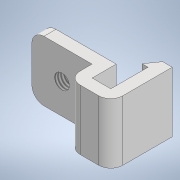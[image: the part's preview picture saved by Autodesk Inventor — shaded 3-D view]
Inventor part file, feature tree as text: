
AUTODESK INVENTOR PART (.ipt)
format: ipt  version: 2021 (Build 250183000, 183)  size: 137,216 bytes
history: native  units: mm
features: sketch x2, other x1, extrude x1, hole x1, fillet x1
ambient origin geometry x8: Origin, YZ Plane, XZ Plane, XY Plane, X Axis, Y Axis, Z Axis, Center Point
bodies: Body1 (feature_tree)
feature tree (6):
  other  "Sólido1"
  extrude  "Extrusão1"  Depth=2.0mm
  hole  "Furo1"  [1 undecoded]
  fillet  "Arredondamento1"  Radius=2.0mm
  sketch  "Esboço1"  dims[d0=2.0mm d1=9.599311mm]
  sketch  "Esboço2"  dims[d2=10.0mm d3=6.2mm d4=2.0mm d5=2.0mm d6=2.0mm d7=3.1mm d8=1.0mm d10=2.0mm d11=2.0mm d12=12.0mm d13=10.0mm d14=0.0mm d15=5.0mm d16=5.0mm d17=2.459mm d18=6.0mm d19=4.0mm d20=2.0mm d21=90.0deg d22=8.0mm d23=20.594885mm d24=2.0mm d25=2.0mm]
note: 1 required parameter value undecoded (feature->parameter linkage not recoverable at this tier; creation-order binding heuristic only, values carry confidence <= 0.55)
